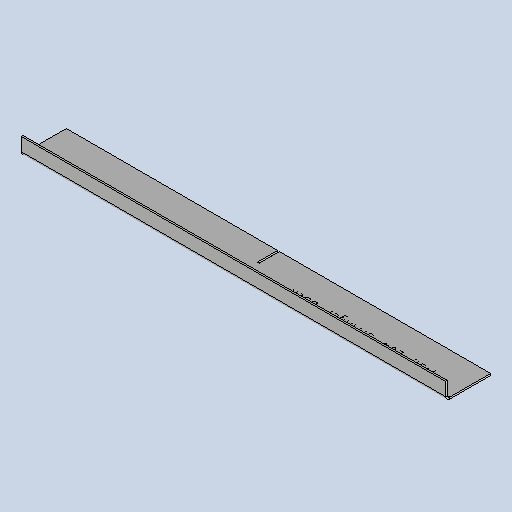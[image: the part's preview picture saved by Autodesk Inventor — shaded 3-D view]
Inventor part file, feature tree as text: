
AUTODESK INVENTOR PART (.ipt)
format: ipt  version: 2025 (Build 290162010, 162A)  size: 275,456 bytes
history: native  units: mm
features: other x5, sheet_metal_op x4, sketch x4, extrude x1
ambient origin geometry x8: Origin, YZ Plane, XZ Plane, XY Plane, X Axis, Y Axis, Z Axis, Center Point
bodies: Solid1 (feature_tree)
feature tree (14):
  sheet_metal_op  "Face1"
  sheet_metal_op  "Flange1"
  extrude  "Extrusion4"  Depth=52.0mm
  other  "Mark3"
  other  "A-Side Definition"
  sketch  "Sketch1"  dims[d0=980.0mm d1=52.0mm]
  other  "Plate1"
  sketch  "Sketch2"  dims[d2=2.0mm]
  other  "Plate2"
  sheet_metal_op  "Bend1"
  sheet_metal_op  "Corner1"
  sketch  "Sketch9"  dims[d3=2.0mm]
  sketch  "Sketch11"  dims[d4=1.0mm d5=4.0mm d6=2.75mm d7=20.0mm d8=90.0deg d9=2.75mm d10=8.0mm d11=2.0mm d12=2.75mm d38=200.0mm d39=12.0mm d44=60.0mm d45=0.0mm d46=0.0mm d47=2.1mm d49=490.0mm d50=29.0mm]
  other  "Definition1"
